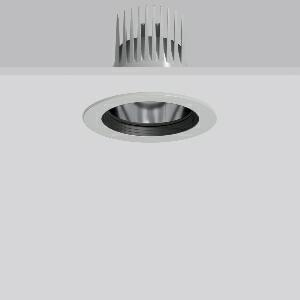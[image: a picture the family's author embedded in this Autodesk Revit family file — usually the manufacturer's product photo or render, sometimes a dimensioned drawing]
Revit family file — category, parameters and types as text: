
# Revit family: heledon_maxi_e_901787_004_2_14d0
name_source: partatom
category: Lighting Fixtures
units: mm (PartAtom-declared; Revit-internal decimal feet)

## family parameters
Cut with Voids When Loaded = No
Host = Face
Light Source = No
Part Type = Normal
Room Calculation Point = No
Round Connector Dimension = Use Diameter
Shared = No

## types (1)
- HELEDON maxi E (1 x LED Modul 927 bakery, 3300 lm, 2700)
    Apparent Load = 33 VA
    Approval mark = CE
    CIE Flux Codes = 96 100 100 100 100
    Color Rendering = 90
    Color Temperature = 2700
    Default Elevation = 1800 mm
    Description = Series: HELEDON maxi
Round recessed downlight. Housing: die-cast aluminium, powder-coated. Black plastic ring and recessed LED to prevent glare from the side. Optical assembly with reflector made of MIRO-Silver with 98% total light reflection for outstanding efficiency - can be changed without tools. Special LED for illumination of pastries included. Suitable for Recessed ceiling mounting. Installation without tools thanks to spring fastening system. Including separate LED converter with connecting cable 600 mm.High quality converter without flickering and stroboscopic effect. Through-wiring box (5 pole) available as accessory. The following accessories can be mounted without use of tools: interchangeable lenses, decorative glasses, honeycomb louvre, clear and frosted diffusers, white interchangeable plastic ring. 
Colour: silver
Diameter: 162 mm
Height: 3 mm
Cut-out diameter: 152 mm
Recess height: 200 mm
Luminaire: recess height: 135 mm
Lamp: LED
Socket: without socket
Colour temperature: bakery
Colour rendering index (CRI): 97
System power: 33 W
Rated luminous flux: 3300 lm
Luminous efficiency: 100 lm/W
Control gear: Regulated power supply
Protection class: II
Type of protection: IP 20
    Height = 0 mm  [stored 0 ft]
    Lamp = 1 x LED Modul 927 bakery
    Lamp Light Flux = 3300 lm
    Lamp count = 1
    Length = 162 mm
    Lifetime = 50000 h
    Luminous efficacy = 100 lm/W
    Manufacturer = RZB
    ModVariant = No
    Model = 901787.004.2
    Mounting Place = Ceiling
    Mounting Type = Recessed
    Number of Poles = 1
    OnlyDefault = Yes
    Power Factor = 1
    Product Name = HELEDON maxi E
    Product group = Recessed downlights
    ProductGroupID = 402
    Protection Class = Protection class II
    Protection Degree = IP 20
    RLX_Detail_Level = 1
    RLX_Emergency_Light_Flux = 0 lm
    RLX_Emergency_Type = 0
    RLX_Emergency_Type_DB = No
    RlxData = <blob elided: 118769 chars, md5=f522da2e>
    Socket = socket
    Standby Power = 0 W
    System Light Flux = 3300 lm
    System Power = 33 W
    Type Comments = Product without accessories
    Type Image = 901662.004.jpg
    URL = http://relux.com
    VarID = ---
    Voltage = 230 V
    Voltage Range = 220-240 V
    Weight = 0.00 kg
    Width = 0 mm  [stored 0 ft]

note: [stored X ft] marks values corroborated as IEEE doubles in the binary element streams (Revit-internal decimal feet)

## geometry (parser evidence)
native form markers: Blend x4, Sweep x11
no freeform markers — native parametric forms only
